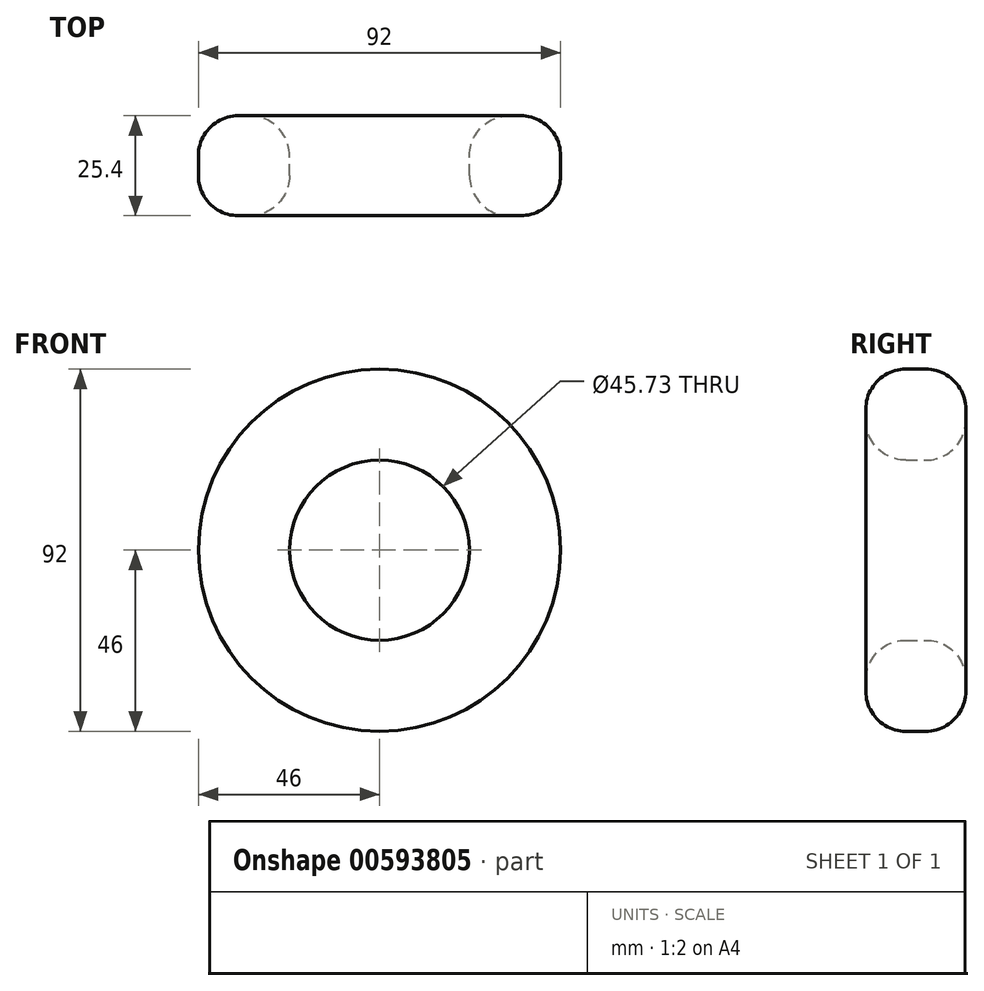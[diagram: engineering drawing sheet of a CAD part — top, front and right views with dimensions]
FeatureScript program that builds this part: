
annotation { "Feature Type Name" : "Feature", "Feature Type Description" : "" }
export const myFeature = defineFeature(function(context is Context, id is Id, definition is map)
    precondition{}
    {
        {
            var Q0;
            Q0=qCreatedBy(makeId("Front.planeOp"),FACE);
            var sketch = newSketch(context, id + "F0", { "sketchPlane" : qUnion([Q0])});
            skCircle(sketch, "E0", {"center": v(0, 0) * mm, "radius": 46 * mm});
            skCircle(sketch, "E1", {"center": v(0, 0) * mm, "radius": 22.87 * mm});
            skSolve(sketch);
        }
        {
            var Q0;
            Q0=makeQuery(id+"F0.imprint","IMPRINT",FACE,{"disambiguationData":[TD([[makeQuery(id+"F0.imprint","IMPRINT",EDGE,{"derivedFrom":sQuery(id+"F0.wireOp",EDGE,"E0")}),1.0]])]});
            extrude(context, id + "F1", {"entities" : qUnion([Q0]), "endBound" : BoundingType.SYMMETRIC, "depth" : 25.4 * mm, "offsetDistance" : 25.4 * mm});
        }
        {
            var Q0;
            Q0=makeQuery(id+"F1.opExtrude","CAP_EDGE",EDGE,{"disambiguationData":[OSD([sQuery(id+"F0.wireOp",EDGE,"E0")])],"isStart":false});
            var Q1;
            Q1=makeQuery(id+"F1.opExtrude","CAP_EDGE",EDGE,{"disambiguationData":[OSD([sQuery(id+"F0.wireOp",EDGE,"E0")])],"isStart":true});
            var Q2;
            Q2=makeQuery(id+"F1.opExtrude","CAP_EDGE",EDGE,{"disambiguationData":[OSD([sQuery(id+"F0.wireOp",EDGE,"E1")])],"isStart":false});
            var Q3;
            Q3=makeQuery(id+"F1.opExtrude","CAP_EDGE",EDGE,{"disambiguationData":[OSD([sQuery(id+"F0.wireOp",EDGE,"E1")])],"isStart":true});
            fillet(context, id + "F2", {"entities" : qUnion([Q0, Q1, Q2, Q3]), "radius" : 10.16 * mm, "tangentPropagation" : true, "allowEdgeOverflow" : false});
        }
    });
